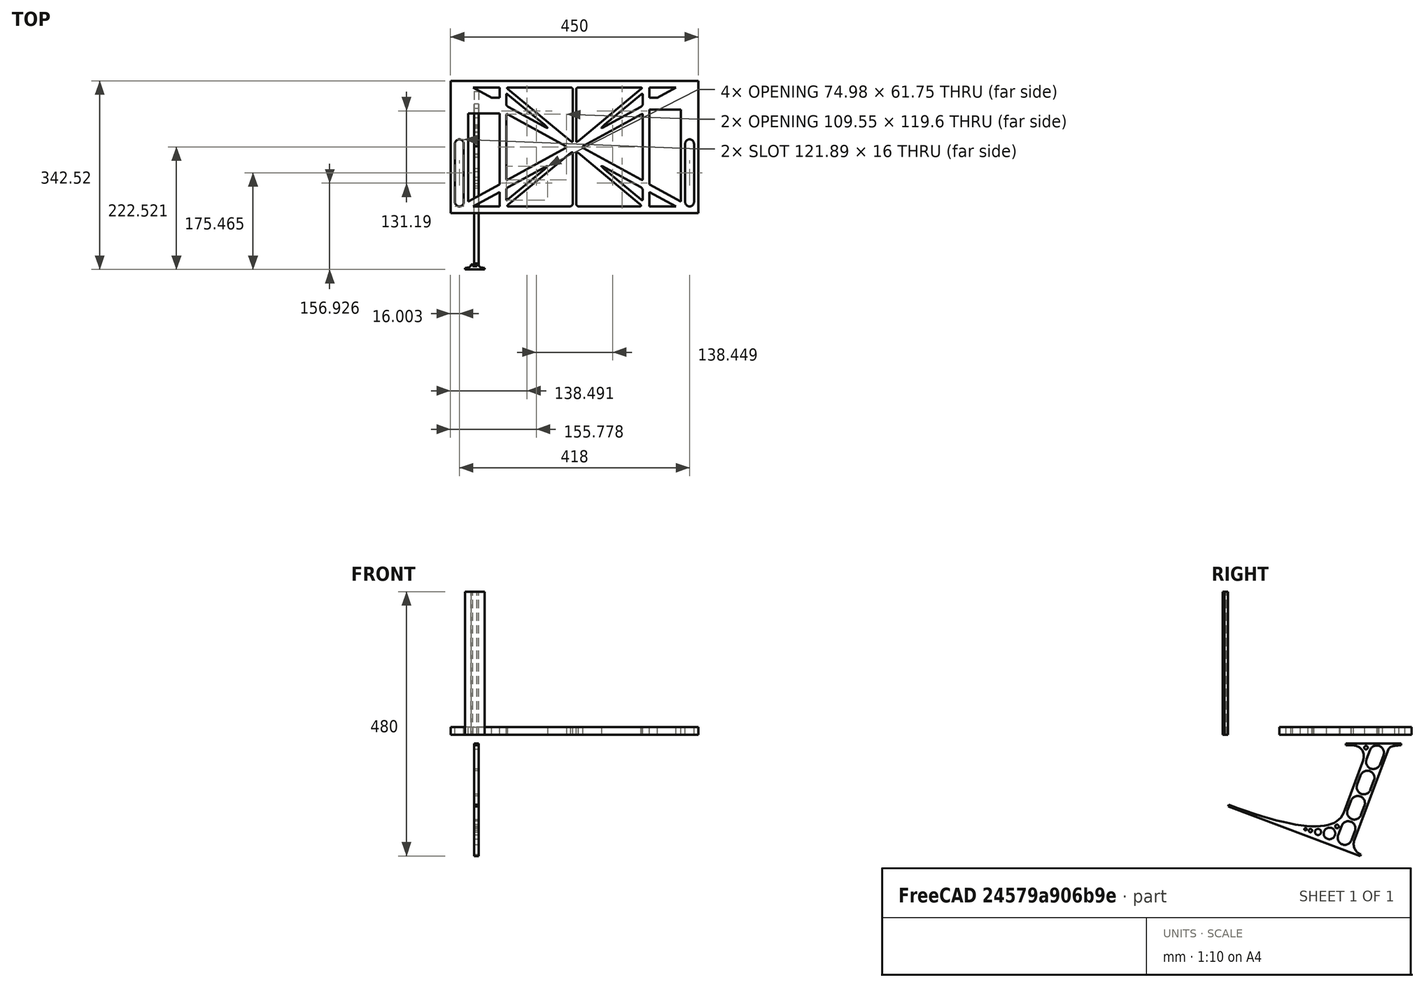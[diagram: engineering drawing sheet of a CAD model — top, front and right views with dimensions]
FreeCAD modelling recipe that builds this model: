
FCSTD DOCUMENT  (FreeCAD 0.19R0.19.2)
Label: laptopStand090
License: All rights reserved
LicenseURL: http://en.wikipedia.org/wiki/All_rights_reserved
objects: Sketcher::SketchObject×3, Part::Extrusion×3
note: 6 computed .brp shape members not serialized (recipe doc carries the construction recipe); baked Part::Feature solids carry a one-line shape summary decoded from their .brp

FEATURE [Sketcher::SketchObject] Sketch
  FullyConstrained = true
  sketch-geometry (248):
    g0: LineSegment StartX=-10.9272 StartY=-82.7794 StartZ=0 EndX=46.0728 EndY=-51.4823 EndZ=0
    g1: LineSegment StartX=366.073 StartY=-91.7794 StartZ=0 EndX=318.073 EndY=-65.424 EndZ=0
    g2: LineSegment StartX=-10.9272 StartY=77.3346 StartZ=0 EndX=-10.9272 EndY=-82.7794 EndZ=0
    g3: LineSegment StartX=375.073 StartY=-82.7794 StartZ=0 EndX=375.073 EndY=83.9235 EndZ=0
    g4: LineSegment StartX=-1.92719 StartY=-91.7794 StartZ=0 EndX=46.0728 EndY=-91.7794 EndZ=0
    g5: LineSegment StartX=318.073 StartY=124.221 StartZ=0 EndX=366.073 EndY=124.221 EndZ=0
    g6: LineSegment StartX=306.073 StartY=77.3346 StartZ=0 EndX=306.073 EndY=-44.8935 EndZ=0
    g7: LineSegment StartX=318.073 StartY=83.9235 StartZ=0 EndX=318.073 EndY=-51.4823 EndZ=0
    g8: LineSegment StartX=318.073 StartY=-51.4823 StartZ=0 EndX=375.073 EndY=-82.7794 EndZ=0
    g9: LineSegment StartX=318.073 StartY=-65.424 StartZ=0 EndX=318.073 EndY=-91.7794 EndZ=0
    g10: LineSegment StartX=318.073 StartY=-91.7794 StartZ=0 EndX=366.073 EndY=-91.7794 EndZ=0
    g11: LineSegment StartX=46.0728 StartY=-65.424 StartZ=0 EndX=-1.92719 EndY=-91.7794 EndZ=0
    g12: LineSegment StartX=46.0728 StartY=-65.424 StartZ=0 EndX=46.0728 EndY=-91.7794 EndZ=0
    g13: LineSegment StartX=46.0728 StartY=77.3346 StartZ=0 EndX=46.0728 EndY=-51.4823 EndZ=0
    g14: LineSegment StartX=-42.9272 StartY=136.221 StartZ=0 EndX=-42.9272 EndY=-103.779 EndZ=0
    g15: LineSegment StartX=407.073 StartY=136.221 StartZ=0 EndX=407.073 EndY=-103.779 EndZ=0
    g16: ArcOfCircle CenterX=-26.9272 CenterY=22.1087 CenterZ=0 NormalX=0 NormalY=0 NormalZ=1 AngleXU=0 Radius=8 StartAngle=1e-16 EndAngle=3.14159
    g17: ArcOfCircle CenterX=-26.9272 CenterY=-83.7794 CenterZ=0 NormalX=0 NormalY=0 NormalZ=1 AngleXU=0 Radius=8 StartAngle=3.14159 EndAngle=6.28319
    g18: LineSegment StartX=-34.9272 StartY=22.1087 StartZ=0 EndX=-34.9272 EndY=-83.7794 EndZ=0
    g19: LineSegment StartX=-18.9272 StartY=22.1087 StartZ=0 EndX=-18.9272 EndY=-83.7794 EndZ=0
    g20: ArcOfCircle CenterX=391.073 CenterY=22.1087 CenterZ=0 NormalX=0 NormalY=0 NormalZ=1 AngleXU=0 Radius=8 StartAngle=-4.4e-15 EndAngle=3.14159
    g21: LineSegment StartX=399.073 StartY=22.1087 StartZ=0 EndX=399.073 EndY=-83.7794 EndZ=0
    g22: LineSegment StartX=383.073 StartY=22.1087 StartZ=0 EndX=383.073 EndY=-83.7794 EndZ=0
    g23: ArcOfCircle CenterX=391.073 CenterY=-83.7794 CenterZ=0 NormalX=0 NormalY=0 NormalZ=1 AngleXU=0 Radius=8 StartAngle=3.14159 EndAngle=6.28319
    g24: Circle CenterX=175.022 CenterY=27.0628 CenterZ=0 NormalX=0 NormalY=0 NormalZ=1 AngleXU=0 Radius=1
    g25: Circle CenterX=179.022 CenterY=24.8665 CenterZ=0 NormalX=0 NormalY=0 NormalZ=1 AngleXU=0 Radius=1
    g26: Circle CenterX=179.022 CenterY=27.0628 CenterZ=0 NormalX=0 NormalY=0 NormalZ=1 AngleXU=0 Radius=1
    g27: BSplineCurve PolesCount=3 KnotsCount=2 Degree=2 IsPeriodic=0
    g28: GeomPoint X=175.022 Y=27.0628 Z=0
    g29: GeomPoint X=179.022 Y=27.0628 Z=0
    g30: Circle CenterX=189.124 CenterY=27.0628 CenterZ=0 NormalX=0 NormalY=0 NormalZ=1 AngleXU=0 Radius=1
    g31: Circle CenterX=185.124 CenterY=24.8665 CenterZ=0 NormalX=0 NormalY=0 NormalZ=1 AngleXU=0 Radius=1
    g32: Circle CenterX=185.124 CenterY=27.0628 CenterZ=0 NormalX=0 NormalY=0 NormalZ=1 AngleXU=0 Radius=1
    g33: BSplineCurve PolesCount=3 KnotsCount=2 Degree=2 IsPeriodic=0
    g34: GeomPoint X=189.124 Y=27.0628 Z=0
    g35: GeomPoint X=185.124 Y=27.0628 Z=0
    g36: Circle CenterX=175.022 CenterY=5.37834 CenterZ=0 NormalX=0 NormalY=0 NormalZ=1 AngleXU=0 Radius=1
    g37: Circle CenterX=179.022 CenterY=7.57463 CenterZ=0 NormalX=0 NormalY=0 NormalZ=1 AngleXU=0 Radius=1
    g38: Circle CenterX=179.022 CenterY=5.34704 CenterZ=0 NormalX=0 NormalY=0 NormalZ=1 AngleXU=0 Radius=1
    g39: BSplineCurve PolesCount=3 KnotsCount=2 Degree=2 IsPeriodic=0
    g40: GeomPoint X=175.022 Y=5.37834 Z=0
    g41: GeomPoint X=179.022 Y=5.34704 Z=0
    g42: Circle CenterX=189.124 CenterY=5.37834 CenterZ=0 NormalX=0 NormalY=0 NormalZ=1 AngleXU=0 Radius=1
    g43: Circle CenterX=185.124 CenterY=7.57463 CenterZ=0 NormalX=0 NormalY=0 NormalZ=1 AngleXU=0 Radius=1
    g44: Circle CenterX=185.124 CenterY=5.34704 CenterZ=0 NormalX=0 NormalY=0 NormalZ=1 AngleXU=0 Radius=1
    g45: BSplineCurve PolesCount=3 KnotsCount=2 Degree=2 IsPeriodic=0
    g46: GeomPoint X=189.124 Y=5.37834 Z=0
    g47: GeomPoint X=185.124 Y=5.34704 Z=0
    g48: Circle CenterX=165.871 CenterY=18.1458 CenterZ=0 NormalX=0 NormalY=0 NormalZ=1 AngleXU=0 Radius=1
    g49: Circle CenterX=169.377 CenterY=16.2206 CenterZ=0 NormalX=0 NormalY=0 NormalZ=1 AngleXU=0 Radius=1
    g50: Circle CenterX=165.871 CenterY=14.2954 CenterZ=0 NormalX=0 NormalY=0 NormalZ=1 AngleXU=0 Radius=1
    g51: BSplineCurve PolesCount=3 KnotsCount=2 Degree=2 IsPeriodic=0
    g52: GeomPoint X=165.871 Y=18.1458 Z=0
    g53: GeomPoint X=165.871 Y=14.2954 Z=0
    g54: Circle CenterX=198.275 CenterY=18.1458 CenterZ=0 NormalX=0 NormalY=0 NormalZ=1 AngleXU=0 Radius=1
    g55: Circle CenterX=194.768 CenterY=16.2206 CenterZ=0 NormalX=0 NormalY=0 NormalZ=1 AngleXU=0 Radius=1
    g56: Circle CenterX=198.275 CenterY=14.2954 CenterZ=0 NormalX=0 NormalY=0 NormalZ=1 AngleXU=0 Radius=1
    g57: BSplineCurve PolesCount=3 KnotsCount=2 Degree=2 IsPeriodic=0
    g58: GeomPoint X=198.275 Y=18.1458 Z=0
    g59: GeomPoint X=198.275 Y=14.2954 Z=0
    g60: LineSegment StartX=198.275 StartY=18.1458 StartZ=0 EndX=306.073 EndY=77.3346 EndZ=0
    g61: LineSegment StartX=198.275 StartY=14.2954 StartZ=0 EndX=306.073 EndY=-44.8935 EndZ=0
    g62: LineSegment StartX=407.073 StartY=-103.779 StartZ=0 EndX=-42.9272 EndY=-103.779 EndZ=0
    g63: LineSegment StartX=407.073 StartY=136.221 StartZ=0 EndX=-42.9272 EndY=136.221 EndZ=0
    g64: LineSegment StartX=46.0728 StartY=77.3346 StartZ=0 EndX=-10.9272 EndY=77.3346 EndZ=0
    g65: LineSegment StartX=46.0728 StartY=105.865 StartZ=0 EndX=31.5028 EndY=105.865 EndZ=0
    g66: LineSegment StartX=46.0728 StartY=124.221 StartZ=0 EndX=46.0728 EndY=105.865 EndZ=0
    g67: LineSegment StartX=-1.92719 StartY=124.221 StartZ=0 EndX=31.5028 EndY=105.865 EndZ=0
    g68: LineSegment StartX=46.0728 StartY=124.221 StartZ=0 EndX=-1.92719 EndY=124.221 EndZ=0
    g69: LineSegment StartX=318.073 StartY=83.9235 StartZ=0 EndX=375.073 EndY=83.9235 EndZ=0
    g70: LineSegment StartX=318.073 StartY=105.865 StartZ=0 EndX=332.643 EndY=105.865 EndZ=0
    g71: LineSegment StartX=332.643 StartY=105.865 StartZ=0 EndX=366.073 EndY=124.221 EndZ=0
    g72: LineSegment StartX=318.073 StartY=124.221 StartZ=0 EndX=318.073 EndY=105.865 EndZ=0
    g73: Circle CenterX=125.607 CenterY=54.1951 CenterZ=0 NormalX=0 NormalY=0 NormalZ=1 AngleXU=0 Radius=1
    g74: Circle CenterX=139.632 CenterY=46.4944 CenterZ=0 NormalX=0 NormalY=0 NormalZ=1 AngleXU=0 Radius=1
    g75: Circle CenterX=127.326 CenterY=56.7187 CenterZ=0 NormalX=0 NormalY=0 NormalZ=1 AngleXU=0 Radius=1
    g76: BSplineCurve PolesCount=3 KnotsCount=2 Degree=2 IsPeriodic=0
    g77: GeomPoint X=125.607 Y=54.1951 Z=0
    g78: GeomPoint X=127.326 Y=56.7187 Z=0
    g79: Circle CenterX=236.821 CenterY=56.7187 CenterZ=0 NormalX=0 NormalY=0 NormalZ=1 AngleXU=0 Radius=1
    g80: Circle CenterX=224.513 CenterY=46.4944 CenterZ=0 NormalX=0 NormalY=0 NormalZ=1 AngleXU=0 Radius=1
    g81: Circle CenterX=238.538 CenterY=54.1951 CenterZ=0 NormalX=0 NormalY=0 NormalZ=1 AngleXU=0 Radius=1
    g82: BSplineCurve PolesCount=3 KnotsCount=2 Degree=2 IsPeriodic=0
    g83: GeomPoint X=236.821 Y=56.7187 Z=0
    g84: GeomPoint X=238.538 Y=54.1951 Z=0
    g85: Circle CenterX=238.538 CenterY=-21.7539 CenterZ=0 NormalX=0 NormalY=0 NormalZ=1 AngleXU=0 Radius=1
    g86: Circle CenterX=224.513 CenterY=-14.0532 CenterZ=0 NormalX=0 NormalY=0 NormalZ=1 AngleXU=0 Radius=1
    g87: Circle CenterX=236.821 CenterY=-24.2775 CenterZ=0 NormalX=0 NormalY=0 NormalZ=1 AngleXU=0 Radius=1
    g88: BSplineCurve PolesCount=3 KnotsCount=2 Degree=2 IsPeriodic=0
    g89: GeomPoint X=238.538 Y=-21.7539 Z=0
    g90: GeomPoint X=236.821 Y=-24.2775 Z=0
    g91: Circle CenterX=125.607 CenterY=-21.7539 CenterZ=0 NormalX=0 NormalY=0 NormalZ=1 AngleXU=0 Radius=1
    g92: Circle CenterX=139.632 CenterY=-14.0532 CenterZ=0 NormalX=0 NormalY=0 NormalZ=1 AngleXU=0 Radius=1
    g93: Circle CenterX=127.325 CenterY=-24.2775 CenterZ=0 NormalX=0 NormalY=0 NormalZ=1 AngleXU=0 Radius=1
    g94: BSplineCurve PolesCount=3 KnotsCount=2 Degree=2 IsPeriodic=0
    g95: GeomPoint X=125.607 Y=-21.7539 Z=0
    g96: GeomPoint X=127.325 Y=-24.2775 Z=0
    g97: Circle CenterX=302.996 CenterY=111.695 CenterZ=0 NormalX=0 NormalY=0 NormalZ=1 AngleXU=0 Radius=1
    g98: Circle CenterX=306.073 CenterY=114.251 CenterZ=0 NormalX=0 NormalY=0 NormalZ=1 AngleXU=0 Radius=1
    g99: Circle CenterX=306.073 CenterY=110.251 CenterZ=0 NormalX=0 NormalY=0 NormalZ=1 AngleXU=0 Radius=1
    g100: BSplineCurve PolesCount=3 KnotsCount=2 Degree=2 IsPeriodic=0
    g101: GeomPoint X=302.996 Y=111.695 Z=0
    g102: GeomPoint X=306.073 Y=110.251 Z=0
    g103: Circle CenterX=306.073 CenterY=95.2763 CenterZ=0 NormalX=0 NormalY=0 NormalZ=1 AngleXU=0 Radius=1
    g104: Circle CenterX=306.073 CenterY=91.2763 CenterZ=0 NormalX=0 NormalY=0 NormalZ=1 AngleXU=0 Radius=1
    g105: Circle CenterX=302.567 CenterY=89.3511 CenterZ=0 NormalX=0 NormalY=0 NormalZ=1 AngleXU=0 Radius=1
    g106: BSplineCurve PolesCount=3 KnotsCount=2 Degree=2 IsPeriodic=0
    g107: GeomPoint X=306.073 Y=95.2763 Z=0
    g108: GeomPoint X=302.567 Y=89.3511 Z=0
    g109: LineSegment StartX=306.073 StartY=110.251 StartZ=0 EndX=306.073 EndY=95.2763 EndZ=0
    g110: LineSegment StartX=302.996 StartY=111.695 StartZ=0 EndX=236.821 EndY=56.7187 EndZ=0
    g111: LineSegment StartX=238.538 StartY=54.1951 StartZ=0 EndX=302.567 EndY=89.3511 EndZ=0
    g112: Circle CenterX=61.1496 CenterY=111.695 CenterZ=0 NormalX=0 NormalY=0 NormalZ=1 AngleXU=0 Radius=1
    g113: Circle CenterX=58.0728 CenterY=114.251 CenterZ=0 NormalX=0 NormalY=0 NormalZ=1 AngleXU=0 Radius=1
    g114: Circle CenterX=58.0728 CenterY=110.251 CenterZ=0 NormalX=0 NormalY=0 NormalZ=1 AngleXU=0 Radius=1
    g115: BSplineCurve PolesCount=3 KnotsCount=2 Degree=2 IsPeriodic=0
    g116: GeomPoint X=61.1496 Y=111.695 Z=0
    g117: GeomPoint X=58.0728 Y=110.251 Z=0
    g118: Circle CenterX=61.5791 CenterY=89.3511 CenterZ=0 NormalX=0 NormalY=0 NormalZ=1 AngleXU=0 Radius=1
    g119: Circle CenterX=58.0728 CenterY=91.2763 CenterZ=0 NormalX=0 NormalY=0 NormalZ=1 AngleXU=0 Radius=1
    g120: Circle CenterX=58.0728 CenterY=95.2763 CenterZ=0 NormalX=0 NormalY=0 NormalZ=1 AngleXU=0 Radius=1
    g121: BSplineCurve PolesCount=3 KnotsCount=2 Degree=2 IsPeriodic=0
    g122: GeomPoint X=61.5791 Y=89.3511 Z=0
    g123: GeomPoint X=58.0728 Y=95.2763 Z=0
    g124: LineSegment StartX=58.0728 StartY=110.251 StartZ=0 EndX=58.0728 EndY=95.2763 EndZ=0
    g125: LineSegment StartX=61.1496 StartY=111.695 StartZ=0 EndX=127.326 EndY=56.7187 EndZ=0
    g126: LineSegment StartX=125.607 StartY=54.1951 StartZ=0 EndX=61.5791 EndY=89.3511 EndZ=0
    g127: Circle CenterX=61.5791 CenterY=-56.9099 CenterZ=0 NormalX=0 NormalY=0 NormalZ=1 AngleXU=0 Radius=1
    g128: Circle CenterX=58.0728 CenterY=-58.8351 CenterZ=0 NormalX=0 NormalY=0 NormalZ=1 AngleXU=0 Radius=1
    g129: Circle CenterX=58.0728 CenterY=-62.8351 CenterZ=0 NormalX=0 NormalY=0 NormalZ=1 AngleXU=0 Radius=1
    g130: BSplineCurve PolesCount=3 KnotsCount=2 Degree=2 IsPeriodic=0
    g131: GeomPoint X=61.5791 Y=-56.9099 Z=0
    g132: GeomPoint X=58.0728 Y=-62.8351 Z=0
    g133: Circle CenterX=58.0728 CenterY=-77.8102 CenterZ=0 NormalX=0 NormalY=0 NormalZ=1 AngleXU=0 Radius=1
    g134: Circle CenterX=58.0728 CenterY=-81.8102 CenterZ=0 NormalX=0 NormalY=0 NormalZ=1 AngleXU=0 Radius=1
    g135: Circle CenterX=61.1496 CenterY=-79.2541 CenterZ=0 NormalX=0 NormalY=0 NormalZ=1 AngleXU=0 Radius=1
    g136: BSplineCurve PolesCount=3 KnotsCount=2 Degree=2 IsPeriodic=0
    g137: GeomPoint X=58.0728 Y=-77.8102 Z=0
    g138: GeomPoint X=61.1496 Y=-79.2541 Z=0
    g139: LineSegment StartX=58.0728 StartY=-62.8351 StartZ=0 EndX=58.0728 EndY=-77.8102 EndZ=0
    g140: LineSegment StartX=61.1496 StartY=-79.2541 StartZ=0 EndX=127.325 EndY=-24.2775 EndZ=0
    g141: LineSegment StartX=125.607 StartY=-21.7539 StartZ=0 EndX=61.5791 EndY=-56.9099 EndZ=0
    g142: Circle CenterX=302.567 CenterY=-56.9099 CenterZ=0 NormalX=0 NormalY=0 NormalZ=1 AngleXU=0 Radius=1
    g143: Circle CenterX=306.073 CenterY=-58.8351 CenterZ=0 NormalX=0 NormalY=0 NormalZ=1 AngleXU=0 Radius=1
    g144: Circle CenterX=306.073 CenterY=-62.8351 CenterZ=0 NormalX=0 NormalY=0 NormalZ=1 AngleXU=0 Radius=1
    g145: BSplineCurve PolesCount=3 KnotsCount=2 Degree=2 IsPeriodic=0
    g146: GeomPoint X=302.567 Y=-56.9099 Z=0
    g147: GeomPoint X=306.073 Y=-62.8351 Z=0
    g148: Circle CenterX=302.996 CenterY=-79.2541 CenterZ=0 NormalX=0 NormalY=0 NormalZ=1 AngleXU=0 Radius=1
    g149: Circle CenterX=306.073 CenterY=-81.8102 CenterZ=0 NormalX=0 NormalY=0 NormalZ=1 AngleXU=0 Radius=1
    g150: Circle CenterX=306.073 CenterY=-77.8102 CenterZ=0 NormalX=0 NormalY=0 NormalZ=1 AngleXU=0 Radius=1
    g151: BSplineCurve PolesCount=3 KnotsCount=2 Degree=2 IsPeriodic=0
    g152: GeomPoint X=302.996 Y=-79.2541 Z=0
    g153: GeomPoint X=306.073 Y=-77.8102 Z=0
    g154: LineSegment StartX=306.073 StartY=-62.8351 StartZ=0 EndX=306.073 EndY=-77.8102 EndZ=0
    g155: LineSegment StartX=302.996 StartY=-79.2541 StartZ=0 EndX=236.821 EndY=-24.2775 EndZ=0
    g156: LineSegment StartX=238.538 StartY=-21.7539 StartZ=0 EndX=302.567 EndY=-56.9099 EndZ=0
    g157: Circle CenterX=61.6457 CenterY=-88.8112 CenterZ=0 NormalX=0 NormalY=0 NormalZ=1 AngleXU=0 Radius=1
    g158: Circle CenterX=58.0728 CenterY=-91.7794 CenterZ=0 NormalX=0 NormalY=0 NormalZ=1 AngleXU=0 Radius=1
    g159: Circle CenterX=63.9135 CenterY=-91.7794 CenterZ=0 NormalX=0 NormalY=0 NormalZ=1 AngleXU=0 Radius=1
    g160: BSplineCurve PolesCount=3 KnotsCount=2 Degree=2 IsPeriodic=0
    g161: GeomPoint X=61.6457 Y=-88.8112 Z=0
    g162: GeomPoint X=63.9135 Y=-91.7794 Z=0
    g163: Circle CenterX=179.022 CenterY=-85.8163 CenterZ=0 NormalX=0 NormalY=0 NormalZ=1 AngleXU=0 Radius=1
    g164: Circle CenterX=179.022 CenterY=-91.7794 CenterZ=0 NormalX=0 NormalY=0 NormalZ=1 AngleXU=0 Radius=1
    g165: Circle CenterX=171.895 CenterY=-91.7794 CenterZ=0 NormalX=0 NormalY=0 NormalZ=1 AngleXU=0 Radius=1
    g166: BSplineCurve PolesCount=3 KnotsCount=2 Degree=2 IsPeriodic=0
    g167: GeomPoint X=179.022 Y=-85.8163 Z=0
    g168: GeomPoint X=171.895 Y=-91.7794 Z=0
    g169: Circle CenterX=185.124 CenterY=-86.2028 CenterZ=0 NormalX=0 NormalY=0 NormalZ=1 AngleXU=0 Radius=1
    g170: Circle CenterX=185.124 CenterY=-91.7794 CenterZ=0 NormalX=0 NormalY=0 NormalZ=1 AngleXU=0 Radius=1
    g171: Circle CenterX=191.747 CenterY=-91.7794 CenterZ=0 NormalX=0 NormalY=0 NormalZ=1 AngleXU=0 Radius=1
    g172: BSplineCurve PolesCount=3 KnotsCount=2 Degree=2 IsPeriodic=0
    g173: GeomPoint X=185.124 Y=-86.2028 Z=0
    g174: GeomPoint X=191.747 Y=-91.7794 Z=0
    g175: Circle CenterX=299.888 CenterY=-86.6413 CenterZ=0 NormalX=0 NormalY=0 NormalZ=1 AngleXU=0 Radius=1
    g176: Circle CenterX=306.073 CenterY=-91.7794 CenterZ=0 NormalX=0 NormalY=0 NormalZ=1 AngleXU=0 Radius=1
    g177: Circle CenterX=298.776 CenterY=-91.7794 CenterZ=0 NormalX=0 NormalY=0 NormalZ=1 AngleXU=0 Radius=1
    g178: BSplineCurve PolesCount=3 KnotsCount=2 Degree=2 IsPeriodic=0
    g179: GeomPoint X=299.888 Y=-86.6413 Z=0
    g180: GeomPoint X=298.776 Y=-91.7794 Z=0
    g181: LineSegment StartX=189.124 StartY=5.37834 StartZ=0 EndX=299.888 EndY=-86.6413 EndZ=0
    g182: LineSegment StartX=298.776 StartY=-91.7794 StartZ=0 EndX=191.747 EndY=-91.7794 EndZ=0
    g183: LineSegment StartX=185.124 StartY=-86.2028 StartZ=0 EndX=185.124 EndY=5.34704 EndZ=0
    g184: LineSegment StartX=179.022 StartY=5.34704 StartZ=0 EndX=179.022 EndY=-85.8163 EndZ=0
    g185: LineSegment StartX=171.895 StartY=-91.7794 StartZ=0 EndX=63.9135 EndY=-91.7794 EndZ=0
    g186: LineSegment StartX=61.6457 StartY=-88.8112 StartZ=0 EndX=175.022 EndY=5.37834 EndZ=0
    g187: Circle CenterX=302.073 CenterY=124.221 CenterZ=0 NormalX=0 NormalY=0 NormalZ=1 AngleXU=0 Radius=1
    g188: Circle CenterX=306.073 CenterY=124.221 CenterZ=0 NormalX=0 NormalY=0 NormalZ=1 AngleXU=0 Radius=1
    g189: Circle CenterX=302.996 CenterY=121.665 CenterZ=0 NormalX=0 NormalY=0 NormalZ=1 AngleXU=0 Radius=1
    g190: BSplineCurve PolesCount=3 KnotsCount=2 Degree=2 IsPeriodic=0
    g191: GeomPoint X=302.073 Y=124.221 Z=0
    g192: GeomPoint X=302.996 Y=121.665 Z=0
    g193: Circle CenterX=189.124 CenterY=124.221 CenterZ=0 NormalX=0 NormalY=0 NormalZ=1 AngleXU=0 Radius=1
    g194: Circle CenterX=185.124 CenterY=124.221 CenterZ=0 NormalX=0 NormalY=0 NormalZ=1 AngleXU=0 Radius=1
    g195: Circle CenterX=185.124 CenterY=120.221 CenterZ=0 NormalX=0 NormalY=0 NormalZ=1 AngleXU=0 Radius=1
    g196: BSplineCurve PolesCount=3 KnotsCount=2 Degree=2 IsPeriodic=0
    g197: GeomPoint X=189.124 Y=124.221 Z=0
    g198: GeomPoint X=185.124 Y=120.221 Z=0
    g199: Circle CenterX=175.022 CenterY=124.221 CenterZ=0 NormalX=0 NormalY=0 NormalZ=1 AngleXU=0 Radius=1
    g200: Circle CenterX=179.022 CenterY=124.221 CenterZ=0 NormalX=0 NormalY=0 NormalZ=1 AngleXU=0 Radius=1
    g201: Circle CenterX=179.022 CenterY=120.221 CenterZ=0 NormalX=0 NormalY=0 NormalZ=1 AngleXU=0 Radius=1
    g202: BSplineCurve PolesCount=3 KnotsCount=2 Degree=2 IsPeriodic=0
    g203: GeomPoint X=175.022 Y=124.221 Z=0
    g204: GeomPoint X=179.022 Y=120.221 Z=0
    g205: Circle CenterX=62.0728 CenterY=124.221 CenterZ=0 NormalX=0 NormalY=0 NormalZ=1 AngleXU=0 Radius=1
    g206: Circle CenterX=58.0728 CenterY=124.221 CenterZ=0 NormalX=0 NormalY=0 NormalZ=1 AngleXU=0 Radius=1
    g207: Circle CenterX=61.1496 CenterY=121.665 CenterZ=0 NormalX=0 NormalY=0 NormalZ=1 AngleXU=0 Radius=1
    g208: BSplineCurve PolesCount=3 KnotsCount=2 Degree=2 IsPeriodic=0
    g209: GeomPoint X=62.0728 Y=124.221 Z=0
    g210: GeomPoint X=61.1496 Y=121.665 Z=0
    g211: LineSegment StartX=62.0728 StartY=124.221 StartZ=0 EndX=175.022 EndY=124.221 EndZ=0
    g212: LineSegment StartX=179.022 StartY=120.221 StartZ=0 EndX=179.022 EndY=27.0628 EndZ=0
    g213: LineSegment StartX=185.124 StartY=27.0628 StartZ=0 EndX=185.124 EndY=120.221 EndZ=0
    g214: LineSegment StartX=189.124 StartY=124.221 StartZ=0 EndX=302.073 EndY=124.221 EndZ=0
    g215: LineSegment StartX=302.996 StartY=121.665 StartZ=0 EndX=189.124 EndY=27.0628 EndZ=0
    g216: LineSegment StartX=175.022 StartY=27.0628 StartZ=0 EndX=61.1496 EndY=121.665 EndZ=0
    g217: Circle CenterX=61.5791 CenterY=75.4095 CenterZ=0 NormalX=0 NormalY=0 NormalZ=1 AngleXU=0 Radius=1
    g218: Circle CenterX=58.0728 CenterY=77.3346 CenterZ=0 NormalX=0 NormalY=0 NormalZ=1 AngleXU=0 Radius=1
    g219: Circle CenterX=58.0728 CenterY=73.3346 CenterZ=0 NormalX=0 NormalY=0 NormalZ=1 AngleXU=0 Radius=1
    g220: BSplineCurve PolesCount=3 KnotsCount=2 Degree=2 IsPeriodic=0
    g221: GeomPoint X=61.5791 Y=75.4095 Z=0
    g222: GeomPoint X=58.0728 Y=73.3346 Z=0
    g223: Circle CenterX=58.0728 CenterY=-40.8935 CenterZ=0 NormalX=0 NormalY=0 NormalZ=1 AngleXU=0 Radius=1
    g224: Circle CenterX=58.0728 CenterY=-44.8935 CenterZ=0 NormalX=0 NormalY=0 NormalZ=1 AngleXU=0 Radius=1
    g225: Circle CenterX=61.5791 CenterY=-42.9683 CenterZ=0 NormalX=0 NormalY=0 NormalZ=1 AngleXU=0 Radius=1
    g226: BSplineCurve PolesCount=3 KnotsCount=2 Degree=2 IsPeriodic=0
    g227: GeomPoint X=58.0728 Y=-40.8935 Z=0
    g228: GeomPoint X=61.5791 Y=-42.9683 Z=0
    g229: LineSegment StartX=61.5791 StartY=-42.9683 StartZ=0 EndX=165.871 EndY=14.2954 EndZ=0
    g230: LineSegment StartX=165.871 StartY=18.1458 StartZ=0 EndX=61.5791 EndY=75.4095 EndZ=0
    g231: LineSegment StartX=58.0728 StartY=73.3346 StartZ=0 EndX=58.0728 EndY=-40.8935 EndZ=0
    g232: LineSegment StartX=306.073 StartY=77.3346 StartZ=0 EndX=306.073 EndY=73.3346 EndZ=0
    g233: LineSegment StartX=306.073 StartY=77.3346 StartZ=0 EndX=302.567 EndY=75.4095 EndZ=0
    g234: LineSegment StartX=306.073 StartY=-44.8935 StartZ=0 EndX=306.073 EndY=-40.8935 EndZ=0
    g235: LineSegment StartX=306.073 StartY=-44.8935 StartZ=0 EndX=302.567 EndY=-42.9683 EndZ=0
    g236: Circle CenterX=302.567 CenterY=-42.9683 CenterZ=0 NormalX=0 NormalY=0 NormalZ=1 AngleXU=0 Radius=1
    g237: Circle CenterX=306.073 CenterY=-44.8935 CenterZ=0 NormalX=0 NormalY=0 NormalZ=1 AngleXU=0 Radius=1
    g238: Circle CenterX=306.073 CenterY=-40.8935 CenterZ=0 NormalX=0 NormalY=0 NormalZ=1 AngleXU=0 Radius=1
    g239: BSplineCurve PolesCount=3 KnotsCount=2 Degree=2 IsPeriodic=0
    g240: GeomPoint X=302.567 Y=-42.9683 Z=0
    g241: GeomPoint X=306.073 Y=-40.8935 Z=0
    g242: Circle CenterX=306.073 CenterY=73.3346 CenterZ=0 NormalX=0 NormalY=0 NormalZ=1 AngleXU=0 Radius=1
    g243: Circle CenterX=306.073 CenterY=77.3346 CenterZ=0 NormalX=0 NormalY=0 NormalZ=1 AngleXU=0 Radius=1
    g244: Circle CenterX=302.567 CenterY=75.4095 CenterZ=0 NormalX=0 NormalY=0 NormalZ=1 AngleXU=0 Radius=1
    g245: BSplineCurve PolesCount=3 KnotsCount=2 Degree=2 IsPeriodic=0
    g246: GeomPoint X=306.073 Y=73.3346 Z=0
    g247: GeomPoint X=302.567 Y=75.4095 Z=0
  constraints (429):
    c: Horizontal(g4)
    c: Horizontal(g5)
    c: Coincident(g7,g8)
    c: Coincident(g9,g1)
    c: Tangent(g7,g9)
    c: Coincident(g12,g11)
    c: Coincident(g0,g13)
    c: Block(g8)
    c: Block(g3)
    c: Block(g1)
    c: Block(g9)
    c: Block(g12)
    c: Block(g11)
    c: Block(g0)
    c: Block(g2)
    c: Block(g6)
    c: Block(g5)
    c: Block(g10)
    c: Block(g4)
    c: Vertical(g14)
    c: Vertical(g15)
    c: Block(g15)
    c: Block(g14)
    c: Tangent(g16,g19) = 1.5708
    c: Tangent(g16,g18) = -1.5708
    c: Tangent(g18,g17) = -1.5708
    c: Tangent(g19,g17) = 1.5708
    c: Vertical(g18)
    c: Equal(g16,g17)
    c: Block(g19)
    c: Block(g18)
    c: Tangent(g20,g21) = 1.5708
    c: Tangent(g21,g23) = 1.5708
    c: Equal(g20,g23)
    c: Coincident(g22,g20)
    c: Coincident(g22,g23)
    c: Block(g21)
    c: Block(g22)
    c: Weight(g24) = 1
    c: Equal(g24,g25)
    c: Equal(g24,g26)
    c: InternalAlignment(g24,g27)
    c: InternalAlignment(g25,g27)
    c: InternalAlignment(g26,g27)
    c: InternalAlignment(g28,g27)
    c: InternalAlignment(g29,g27)
    c: Weight(g30) = 1
    c: Equal(g30,g31)
    c: Equal(g30,g32)
    c: InternalAlignment(g30,g33)
    c: InternalAlignment(g31,g33)
    c: InternalAlignment(g32,g33)
    c: InternalAlignment(g34,g33)
    c: InternalAlignment(g35,g33)
    c: Block(g33)
    c: Block(g27)
    c: Weight(g36) = 1
    c: Equal(g36,g37)
    c: Equal(g36,g38)
    c: InternalAlignment(g36,g39)
    c: InternalAlignment(g37,g39)
    c: InternalAlignment(g38,g39)
    c: InternalAlignment(g40,g39)
    c: InternalAlignment(g41,g39)
    c: Weight(g42) = 1
    c: Equal(g42,g43)
    c: Equal(g42,g44)
    c: InternalAlignment(g42,g45)
    c: InternalAlignment(g43,g45)
    c: InternalAlignment(g44,g45)
    c: InternalAlignment(g46,g45)
    c: InternalAlignment(g47,g45)
    c: Block(g45)
    c: Block(g39)
    c: Weight(g48) = 1
    c: Equal(g48,g49)
    c: Equal(g48,g50)
    c: InternalAlignment(g48,g51)
    c: InternalAlignment(g49,g51)
    c: InternalAlignment(g50,g51)
    c: InternalAlignment(g52,g51)
    c: InternalAlignment(g53,g51)
    c: Weight(g54) = 1
    c: Equal(g54,g55)
    c: Equal(g54,g56)
    c: InternalAlignment(g54,g57)
    c: InternalAlignment(g55,g57)
    c: InternalAlignment(g56,g57)
    c: InternalAlignment(g58,g57)
    c: InternalAlignment(g59,g57)
    c: Block(g51)
    c: Block(g57)
    c: Coincident(g60,g57)
    c: Coincident(g60,g6)
    c: Coincident(g61,g57)
    c: Coincident(g61,g6)
    c: Coincident(g62,g15)
    c: Coincident(g62,g14)
    c: Horizontal(g62)
    c: Distance(g62) = 450
    c: Coincident(g63,g15)
    c: Coincident(g63,g14)
    c: Horizontal(g63)
    c: Horizontal(g64)
    c: Coincident(g13,g64)
    c: Horizontal(g65)
    c: Vertical(g66)
    c: Block(g66)
    c: Block(g65)
    c: Block(g64)
    c: Distance(g66) = 18.3554
    c: Coincident(g68,g66)
    c: Coincident(g68,g67)
    c: Horizontal(g68)
    c: Block(g68)
    c: Block(g67)
    c: Coincident(g65,g67)
    c: Coincident(g2,g64)
    c: Coincident(g69,g7)
    c: Horizontal(g69)
    c: Horizontal(g70)
    c: Block(g69)
    c: Coincident(g71,g5)
    c: Coincident(g72,g5)
    c: Coincident(g72,g70)
    c: Vertical(g72)
    c: Block(g72)
    c: Coincident(g70,g71)
    c: Block(g71)
    c: Coincident(g3,g69)
    c: Weight(g73) = 1
    c: Equal(g73,g74)
    c: Equal(g73,g75)
    c: InternalAlignment(g73,g76)
    c: InternalAlignment(g74,g76)
    c: InternalAlignment(g75,g76)
    c: InternalAlignment(g77,g76)
    c: InternalAlignment(g78,g76)
    c: Block(g76)
    c: Weight(g79) = 1
    c: Equal(g79,g80)
    c: Equal(g79,g81)
    c: InternalAlignment(g79,g82)
    c: InternalAlignment(g80,g82)
    c: InternalAlignment(g81,g82)
    c: InternalAlignment(g83,g82)
    c: InternalAlignment(g84,g82)
    c: Block(g82)
    c: Weight(g85) = 1
    c: Equal(g85,g86)
    c: Equal(g85,g87)
    c: InternalAlignment(g85,g88)
    c: InternalAlignment(g86,g88)
    c: InternalAlignment(g87,g88)
    c: InternalAlignment(g89,g88)
    c: InternalAlignment(g90,g88)
    c: Block(g88)
    c: Weight(g91) = 1
    c: Equal(g91,g92)
    c: Equal(g91,g93)
    c: InternalAlignment(g91,g94)
    c: InternalAlignment(g92,g94)
    c: InternalAlignment(g93,g94)
    c: InternalAlignment(g95,g94)
    c: InternalAlignment(g96,g94)
    c: Block(g94)
    c: Weight(g97) = 1
    c: Equal(g97,g98)
    c: Equal(g97,g99)
    c: InternalAlignment(g97,g100)
    c: InternalAlignment(g98,g100)
    c: InternalAlignment(g99,g100)
    c: InternalAlignment(g101,g100)
    c: InternalAlignment(g102,g100)
    c: Weight(g103) = 1
    c: Equal(g103,g104)
    c: Equal(g103,g105)
    c: InternalAlignment(g103,g106)
    c: InternalAlignment(g104,g106)
    c: InternalAlignment(g105,g106)
    c: InternalAlignment(g107,g106)
    c: InternalAlignment(g108,g106)
    c: Block(g100)
    c: Block(g106)
    c: Coincident(g109,g100)
    c: Coincident(g109,g106)
    c: Vertical(g109)
    c: Coincident(g110,g100)
    c: Coincident(g110,g82)
    c: Coincident(g111,g82)
    c: Coincident(g111,g106)
    c: Weight(g112) = 1
    c: Equal(g112,g113)
    c: Equal(g112,g114)
    c: InternalAlignment(g112,g115)
    c: InternalAlignment(g113,g115)
    c: InternalAlignment(g114,g115)
    c: InternalAlignment(g116,g115)
    c: InternalAlignment(g117,g115)
    c: Weight(g118) = 1
    c: Equal(g118,g119)
    c: Equal(g118,g120)
    c: InternalAlignment(g118,g121)
    c: InternalAlignment(g119,g121)
    c: InternalAlignment(g120,g121)
    c: InternalAlignment(g122,g121)
    c: InternalAlignment(g123,g121)
    c: Block(g115)
    c: Block(g121)
    c: Coincident(g124,g115)
    c: Coincident(g124,g121)
    c: Vertical(g124)
    c: Coincident(g125,g115)
    c: Coincident(g125,g76)
    c: Coincident(g126,g76)
    c: Coincident(g126,g121)
    c: Weight(g127) = 1
    c: Equal(g127,g128)
    c: Equal(g127,g129)
    c: InternalAlignment(g127,g130)
    c: InternalAlignment(g128,g130)
    c: InternalAlignment(g129,g130)
    c: InternalAlignment(g131,g130)
    c: InternalAlignment(g132,g130)
    c: Weight(g133) = 1
    c: Equal(g133,g134)
    c: Equal(g133,g135)
    c: InternalAlignment(g133,g136)
    c: InternalAlignment(g134,g136)
    c: InternalAlignment(g135,g136)
    c: InternalAlignment(g137,g136)
    c: InternalAlignment(g138,g136)
    c: Block(g130)
    c: Block(g136)
    c: Coincident(g139,g130)
    c: Coincident(g139,g136)
    c: Vertical(g139)
    c: Coincident(g140,g136)
    c: Coincident(g140,g94)
    c: Coincident(g141,g94)
    c: Coincident(g141,g130)
    c: Weight(g142) = 1
    c: Equal(g142,g143)
    c: Equal(g142,g144)
    c: InternalAlignment(g142,g145)
    c: InternalAlignment(g143,g145)
    c: InternalAlignment(g144,g145)
    c: InternalAlignment(g146,g145)
    c: InternalAlignment(g147,g145)
    c: Weight(g148) = 1
    c: Equal(g148,g149)
    c: Equal(g148,g150)
    c: InternalAlignment(g148,g151)
    c: InternalAlignment(g149,g151)
    c: InternalAlignment(g150,g151)
    c: InternalAlignment(g152,g151)
    c: InternalAlignment(g153,g151)
    c: Block(g145)
    c: Block(g151)
    c: Coincident(g154,g145)
    c: Coincident(g154,g151)
    c: Vertical(g154)
    c: Coincident(g155,g151)
    c: Coincident(g155,g88)
    c: Coincident(g156,g88)
    c: Coincident(g156,g145)
    c: Weight(g157) = 1
    c: Equal(g157,g158)
    c: Equal(g157,g159)
    c: InternalAlignment(g157,g160)
    c: InternalAlignment(g158,g160)
    c: InternalAlignment(g159,g160)
    c: InternalAlignment(g161,g160)
    c: InternalAlignment(g162,g160)
    c: Weight(g163) = 1
    c: Equal(g163,g164)
    c: Equal(g163,g165)
    c: InternalAlignment(g163,g166)
    c: InternalAlignment(g164,g166)
    c: InternalAlignment(g165,g166)
    c: InternalAlignment(g167,g166)
    c: InternalAlignment(g168,g166)
    c: Weight(g169) = 1
    c: Equal(g169,g170)
    c: Equal(g169,g171)
    c: InternalAlignment(g169,g172)
    c: InternalAlignment(g170,g172)
    c: InternalAlignment(g171,g172)
    c: InternalAlignment(g173,g172)
    c: InternalAlignment(g174,g172)
    c: Weight(g175) = 1
    c: Equal(g175,g176)
    c: Equal(g175,g177)
    c: InternalAlignment(g175,g178)
    c: InternalAlignment(g176,g178)
    c: InternalAlignment(g177,g178)
    c: InternalAlignment(g179,g178)
    c: InternalAlignment(g180,g178)
    c: Block(g178)
    c: Block(g172)
    c: Block(g166)
    c: Block(g160)
    c: Coincident(g181,g45)
    c: Coincident(g181,g178)
    c: Coincident(g182,g178)
    c: Coincident(g182,g172)
    c: Horizontal(g182)
    c: Coincident(g183,g172)
    c: Coincident(g183,g45)
    c: Vertical(g183)
    c: Coincident(g184,g39)
    c: Coincident(g184,g166)
    c: Vertical(g184)
    c: Coincident(g185,g166)
    c: Coincident(g185,g160)
    c: Horizontal(g185)
    c: Coincident(g186,g160)
    c: Coincident(g186,g39)
    c: Weight(g187) = 1
    c: Equal(g187,g188)
    c: Equal(g187,g189)
    c: InternalAlignment(g187,g190)
    c: InternalAlignment(g188,g190)
    c: InternalAlignment(g189,g190)
    c: InternalAlignment(g191,g190)
    c: InternalAlignment(g192,g190)
    c: Weight(g193) = 1
    c: Equal(g193,g194)
    c: Equal(g193,g195)
    c: InternalAlignment(g193,g196)
    c: InternalAlignment(g194,g196)
    c: InternalAlignment(g195,g196)
    c: InternalAlignment(g197,g196)
    c: InternalAlignment(g198,g196)
    c: Weight(g199) = 1
    c: Equal(g199,g200)
    c: Equal(g199,g201)
    c: InternalAlignment(g199,g202)
    c: InternalAlignment(g200,g202)
    c: InternalAlignment(g201,g202)
    c: InternalAlignment(g203,g202)
    c: InternalAlignment(g204,g202)
    c: Weight(g205) = 1
    c: Equal(g205,g206)
    c: Equal(g205,g207)
    c: InternalAlignment(g205,g208)
    c: InternalAlignment(g206,g208)
    c: InternalAlignment(g207,g208)
    c: InternalAlignment(g209,g208)
    c: InternalAlignment(g210,g208)
    c: Block(g208)
    c: Block(g202)
    c: Block(g196)
    c: Block(g190)
    c: Coincident(g211,g208)
    c: Coincident(g211,g202)
    c: Horizontal(g211)
    c: Coincident(g212,g202)
    c: Coincident(g212,g27)
    c: Vertical(g212)
    c: Coincident(g213,g33)
    c: Coincident(g213,g196)
    c: Vertical(g213)
    c: Coincident(g214,g196)
    c: Coincident(g214,g190)
    c: Horizontal(g214)
    c: Coincident(g215,g190)
    c: Coincident(g215,g33)
    c: Coincident(g216,g27)
    c: Coincident(g216,g208)
    c: Weight(g217) = 1
    c: Equal(g217,g218)
    c: Equal(g217,g219)
    c: InternalAlignment(g217,g220)
    c: InternalAlignment(g218,g220)
    c: InternalAlignment(g219,g220)
    c: InternalAlignment(g221,g220)
    c: InternalAlignment(g222,g220)
    c: Weight(g223) = 1
    c: Equal(g223,g224)
    c: Equal(g223,g225)
    c: InternalAlignment(g223,g226)
    c: InternalAlignment(g224,g226)
    c: InternalAlignment(g225,g226)
    c: InternalAlignment(g227,g226)
    c: InternalAlignment(g228,g226)
    c: Block(g226)
    c: Block(g220)
    c: Coincident(g229,g226)
    c: Coincident(g229,g51)
    c: Coincident(g230,g51)
    c: Coincident(g230,g220)
    c: Coincident(g231,g220)
    c: Coincident(g231,g226)
    c: Vertical(g231)
    c: Vertical(g232)
    c: Vertical(g234)
    c: Parallel(g61,g235)
    c: Parallel(g233,g60)
    c: Distance(g233) = 4
    c: Distance(g232) = 4
    c: Distance(g234) = 4
    c: Distance(g235) = 4
    c: Coincident(g233,g232)
    c: Coincident(g6,g232)
    c: Coincident(g234,g6)
    c: Coincident(g235,g6)
    c: Coincident(g239,g235)
    c: Weight(g236) = 1
    c: Equal(g236,g237)
    c: Coincident(g237,g6)
    c: Equal(g236,g238)
    c: Coincident(g239,g234)
    c: InternalAlignment(g236,g239)
    c: InternalAlignment(g237,g239)
    c: InternalAlignment(g238,g239)
    c: InternalAlignment(g240,g239)
    c: InternalAlignment(g241,g239)
    c: Coincident(g245,g232)
    c: Weight(g242) = 1
    c: Equal(g242,g243)
    c: Coincident(g243,g6)
    c: Equal(g242,g244)
    c: Coincident(g245,g233)
    c: InternalAlignment(g242,g245)
    c: InternalAlignment(g243,g245)
    c: InternalAlignment(g244,g245)
    c: InternalAlignment(g246,g245)
    c: InternalAlignment(g247,g245)
FEATURE [Sketcher::SketchObject] Sketch001
  FullyConstrained = true
  MapMode = 4
  Placement = pos=(0,0,0) rot=(0.57735,0.57735,0.57735;2.0944rad)
  Support = -> [Sketch]
  sketch-geometry (46):
    g0: BSplineCurve PolesCount=3 KnotsCount=2 Degree=2 IsPeriodic=0
    g1: ArcOfCircle CenterX=73.1223 CenterY=-32.291 CenterZ=0 NormalX=0 NormalY=0 NormalZ=1 AngleXU=0 Radius=13 StartAngle=5.92268 EndAngle=9.06428
    g2: ArcOfCircle CenterX=66.7816 CenterY=-49.1439 CenterZ=0 NormalX=0 NormalY=0 NormalZ=1 AngleXU=0 Radius=13 StartAngle=2.78068 EndAngle=5.92131
    g3: ArcOfCircle CenterX=55.9263 CenterY=-78.1807 CenterZ=0 NormalX=0 NormalY=0 NormalZ=1 AngleXU=0 Radius=13 StartAngle=5.92268 EndAngle=9.06428
    g4: ArcOfCircle CenterX=49.5884 CenterY=-95.0342 CenterZ=0 NormalX=0 NormalY=0 NormalZ=1 AngleXU=0 Radius=13 StartAngle=2.78068 EndAngle=5.92131
    g5: ArcOfCircle CenterX=38.7206 CenterY=-124.067 CenterZ=0 NormalX=0 NormalY=0 NormalZ=1 AngleXU=0 Radius=13 StartAngle=5.92268 EndAngle=9.06428
    g6: ArcOfCircle CenterX=32.3875 CenterY=-140.92 CenterZ=0 NormalX=0 NormalY=0 NormalZ=1 AngleXU=0 Radius=13 StartAngle=2.78068 EndAngle=5.92131
    g7: ArcOfCircle CenterX=21.4715 CenterY=-169.934 CenterZ=0 NormalX=0 NormalY=0 NormalZ=1 AngleXU=0 Radius=13 StartAngle=5.92268 EndAngle=9.06428
    g8: ArcOfCircle CenterX=15.1336 CenterY=-186.787 CenterZ=0 NormalX=0 NormalY=0 NormalZ=1 AngleXU=0 Radius=13 StartAngle=2.78068 EndAngle=5.92131
    g9-g12: Circle x4 (B-spline internal-alignment scaffolding for g13; pole/knot coordinates omitted)
    g13: BSplineCurve PolesCount=4 KnotsCount=2 Degree=3 IsPeriodic=0
    g14: GeomPoint X=28.8094 Y=-19.0875 Z=0
    g15: GeomPoint X=47.0443 Y=-50.4712 Z=0
    g16: Circle CenterX=53.5586 CenterY=-23.2695 CenterZ=0 NormalX=0 NormalY=0 NormalZ=1 AngleXU=0 Radius=3.24518
    g17: Circle CenterX=-195.441 CenterY=-127.082 CenterZ=0 NormalX=0 NormalY=0 NormalZ=1 AngleXU=0 Radius=1
    g18: Circle CenterX=-8.24091 CenterY=-197.481 CenterZ=0 NormalX=0 NormalY=0 NormalZ=1 AngleXU=0 Radius=1
    g19: Circle CenterX=12.8789 CenterY=-141.321 CenterZ=0 NormalX=0 NormalY=0 NormalZ=1 AngleXU=0 Radius=1
    g20: BSplineCurve PolesCount=3 KnotsCount=2 Degree=2 IsPeriodic=0
    g21: GeomPoint X=-195.441 Y=-127.082 Z=0
    g22: GeomPoint X=12.8789 Y=-141.321 Z=0
    g23: Circle CenterX=-12.8016 CenterY=-179.036 CenterZ=0 NormalX=0 NormalY=0 NormalZ=1 AngleXU=0 Radius=10.5072
    g24: Circle CenterX=0.933922 CenterY=-166.43 CenterZ=0 NormalX=0 NormalY=0 NormalZ=1 AngleXU=0 Radius=3.26661
    g25: Circle CenterX=-33.5518 CenterY=-176.44 CenterZ=0 NormalX=0 NormalY=0 NormalZ=1 AngleXU=0 Radius=5.64388
    g26: Circle CenterX=-47.2366 CenterY=-173.859 CenterZ=0 NormalX=0 NormalY=0 NormalZ=1 AngleXU=0 Radius=3.01653
    g27: Circle CenterX=-56.2595 CenterY=-171.456 CenterZ=0 NormalX=0 NormalY=0 NormalZ=1 AngleXU=0 Radius=2.12826
    g28: ArcOfCircle CenterX=51.2151 CenterY=-198.473 CenterZ=0 NormalX=0 NormalY=0 NormalZ=1 AngleXU=0 Radius=20 StartAngle=2.78189 EndAngle=4.35269
    g29: LineSegment StartX=32.4951 StartY=-191.433 StartZ=0 EndX=94.6578 EndY=-26.1352 EndZ=0
    g30: LineSegment StartX=43.1192 StartY=-220.001 StartZ=0 EndX=-196.497 EndY=-129.89 EndZ=0
    g31: LineSegment StartX=43.1192 StartY=-220.001 StartZ=0 EndX=44.1752 EndY=-217.193 EndZ=0
    g32: LineSegment StartX=117.223 StartY=-19.0875 StartZ=0 EndX=117.223 EndY=-16.0875 EndZ=0
    g33: LineSegment StartX=117.223 StartY=-16.0875 StartZ=0 EndX=17.2232 EndY=-16.0875 EndZ=0
    g34: LineSegment StartX=17.2232 StartY=-16.0875 StartZ=0 EndX=17.2232 EndY=-19.0875 EndZ=0
    g35: LineSegment StartX=28.8094 StartY=-19.0875 StartZ=0 EndX=17.2232 EndY=-19.0875 EndZ=0
    g36: LineSegment StartX=47.0443 StartY=-50.4712 StartZ=0 EndX=12.8789 EndY=-141.321 EndZ=0
    g37: LineSegment StartX=-195.441 StartY=-127.082 StartZ=0 EndX=-196.497 EndY=-129.89 EndZ=0
    g38: LineSegment StartX=85.2866 StartY=-36.8766 StartZ=0 EndX=78.9396 EndY=-53.7463 EndZ=0
    g39: LineSegment StartX=60.9579 StartY=-27.7053 StartZ=0 EndX=54.6191 EndY=-44.5532 EndZ=0
    g40: LineSegment StartX=68.0907 StartY=-82.7664 StartZ=0 EndX=61.7465 EndY=-99.6365 EndZ=0
    g41: LineSegment StartX=43.7619 StartY=-73.595 StartZ=0 EndX=37.426 EndY=-90.4435 EndZ=0
    g42: LineSegment StartX=50.885 StartY=-128.652 StartZ=0 EndX=44.5456 EndY=-145.522 EndZ=0
    g43: LineSegment StartX=26.5562 StartY=-119.481 StartZ=0 EndX=20.2251 EndY=-136.329 EndZ=0
    g44: LineSegment StartX=9.3071 StartY=-165.349 StartZ=0 EndX=2.97115 EndY=-182.197 EndZ=0
    g45: LineSegment StartX=33.6358 StartY=-174.52 StartZ=0 EndX=27.2917 EndY=-191.39 EndZ=0
  constraints (71):
    c: Block(g0)
    c: Block(g1)
    c: Block(g2)
    c: Block(g4)
    c: Block(g3)
    c: Block(g6)
    c: Block(g5)
    c: Block(g8)
    c: Block(g7)
    c: Weight(g9) = 1
    c: Equal(g9,g10)
    c: Equal(g9,g11)
    c: Equal(g9,g12)
    c: InternalAlignment(g9-g12 -> g13) x4
    c: InternalAlignment(g14,g13)
    c: InternalAlignment(g15,g13)
    c: Block(g16)
    c: Weight(g17) = 1
    c: Equal(g17,g18)
    c: Equal(g17,g19)
    c: InternalAlignment(g17,g20)
    c: InternalAlignment(g18,g20)
    c: InternalAlignment(g19,g20)
    c: InternalAlignment(g21,g20)
    c: InternalAlignment(g22,g20)
    c: Block(g20)
    c: Block(g23)
    c: Block(g24)
    c: Block(g25)
    c: Block(g26)
    c: Block(g27)
    c: Block(g28)
    c: Coincident(g29,g28)
    c: Coincident(g29,g0)
    c: Block(g13)
    c: Coincident(g31,g30)
    c: Coincident(g31,g28)
    c: Block(g31)
    c: Coincident(g32,g0)
    c: Vertical(g32)
    c: Coincident(g33,g32)
    c: Horizontal(g33)
    c: Coincident(g34,g33)
    c: Vertical(g34)
    c: Block(g33)
    c: Coincident(g35,g13)
    c: Coincident(g35,g34)
    c: Horizontal(g35)
    c: Coincident(g36,g13)
    c: Coincident(g36,g20)
    c: Coincident(g37,g20)
    c: Coincident(g37,g30)
    c: Block(g30)
    c: Coincident(g38,g1)
    c: Coincident(g38,g2)
    c: Coincident(g39,g1)
    c: Coincident(g39,g2)
    c: Coincident(g40,g3)
    c: Coincident(g40,g4)
    c: Coincident(g41,g3)
    c: Coincident(g41,g4)
    c: Coincident(g42,g5)
    c: Coincident(g42,g6)
    c: Coincident(g43,g5)
    c: Coincident(g43,g6)
    c: Coincident(g44,g7)
    c: Coincident(g44,g8)
    c: Coincident(g45,g7)
    c: Coincident(g45,g8)
    c: Distance(g30) = 256
    c: Distance(g33) = 100
FEATURE [Part::Extrusion] Extrude002
  Base = -> Sketch001
  Dir = (1,0,0)
  DirMode = 2
  FaceMakerClass = Part::FaceMakerBullseye
  LengthFwd = 8
  LengthRev = 0
  Solid = true
  Symmetric = false
FEATURE [Sketcher::SketchObject] Sketch002
  FullyConstrained = true
  sketch-geometry (20):
    g0: LineSegment StartX=-2.77179 StartY=-200.304 StartZ=0 EndX=5.22821 EndY=-200.304 EndZ=0
    g1: LineSegment StartX=5.22821 StartY=-200.304 StartZ=0 EndX=5.22821 EndY=-197.304 EndZ=0
    g2: LineSegment StartX=-2.77179 StartY=-200.304 StartZ=0 EndX=-2.77179 EndY=-197.304 EndZ=0
    g3: LineSegment StartX=5.22821 StartY=-197.304 StartZ=0 EndX=8.22821 EndY=-197.304 EndZ=0
    g4: LineSegment StartX=-2.77179 StartY=-197.304 StartZ=0 EndX=-5.77179 EndY=-197.304 EndZ=0
    g5: LineSegment StartX=19.2282 StartY=-203.304 StartZ=0 EndX=19.2282 EndY=-206.304 EndZ=0
    g6: LineSegment StartX=-16.7718 StartY=-203.304 StartZ=0 EndX=-16.7718 EndY=-206.304 EndZ=0
    g7: LineSegment StartX=-16.7718 StartY=-206.304 StartZ=0 EndX=19.2282 EndY=-206.304 EndZ=0
    g8: Circle CenterX=-16.7718 CenterY=-203.304 CenterZ=0 NormalX=0 NormalY=0 NormalZ=1 AngleXU=0 Radius=1
    g9: Circle CenterX=-5.77179 CenterY=-203.304 CenterZ=0 NormalX=0 NormalY=0 NormalZ=1 AngleXU=0 Radius=1
    g10: Circle CenterX=-5.77179 CenterY=-197.304 CenterZ=0 NormalX=0 NormalY=0 NormalZ=1 AngleXU=0 Radius=1
    g11: BSplineCurve PolesCount=3 KnotsCount=2 Degree=2 IsPeriodic=0
    g12: GeomPoint X=-16.7718 Y=-203.304 Z=0
    g13: GeomPoint X=-5.77179 Y=-197.304 Z=0
    g14: Circle CenterX=19.2282 CenterY=-203.304 CenterZ=0 NormalX=0 NormalY=0 NormalZ=1 AngleXU=0 Radius=1
    g15: Circle CenterX=8.22821 CenterY=-203.304 CenterZ=0 NormalX=0 NormalY=0 NormalZ=1 AngleXU=0 Radius=1
    g16: Circle CenterX=8.22821 CenterY=-197.304 CenterZ=0 NormalX=0 NormalY=0 NormalZ=1 AngleXU=0 Radius=1
    g17: BSplineCurve PolesCount=3 KnotsCount=2 Degree=2 IsPeriodic=0
    g18: GeomPoint X=19.2282 Y=-203.304 Z=0
    g19: GeomPoint X=8.22821 Y=-197.304 Z=0
  constraints (41):
    c: Horizontal(g0)
    c: Distance(g0) = 8
    c: Coincident(g1,g0)
    c: Vertical(g1)
    c: Distance(g1) = 3
    c: Coincident(g2,g0)
    c: Vertical(g2)
    c: Distance(g2) = 3
    c: Coincident(g3,g1)
    c: Horizontal(g3)
    c: Distance(g3) = 3
    c: Coincident(g4,g2)
    c: Horizontal(g4)
    c: Distance(g4) = 3
    c: Vertical(g5)
    c: Vertical(g6)
    c: Coincident(g7,g6)
    c: Coincident(g7,g5)
    c: Weight(g8) = 1
    c: Equal(g8,g9)
    c: Equal(g8,g10)
    c: Coincident(g11,g4)
    c: InternalAlignment(g8,g11)
    c: InternalAlignment(g9,g11)
    c: InternalAlignment(g10,g11)
    c: InternalAlignment(g12,g11)
    c: InternalAlignment(g13,g11)
    c: Coincident(g17,g5)
    c: Weight(g14) = 1
    c: Equal(g14,g15)
    c: Equal(g14,g16)
    c: Coincident(g17,g3)
    c: InternalAlignment(g14,g17)
    c: InternalAlignment(g15,g17)
    c: InternalAlignment(g16,g17)
    c: InternalAlignment(g18,g17)
    c: InternalAlignment(g19,g17)
    c: Block(g7)
    c: Block(g17)
    c: Block(g11)
    c: Block(g6)
FEATURE [Part::Extrusion] Extrude003
  Base = -> Sketch002
  Dir = (0,0,1)
  DirMode = 2
  FaceMakerClass = Part::FaceMakerBullseye
  LengthFwd = 260
  LengthRev = 0
  Solid = true
  Symmetric = false
FEATURE [Part::Extrusion] Extrude
  Base = -> Sketch
  Dir = (0,0,1)
  DirMode = 2
  FaceMakerClass = Part::FaceMakerBullseye
  LengthFwd = 14
  LengthRev = 0
  Solid = true
  Symmetric = false
